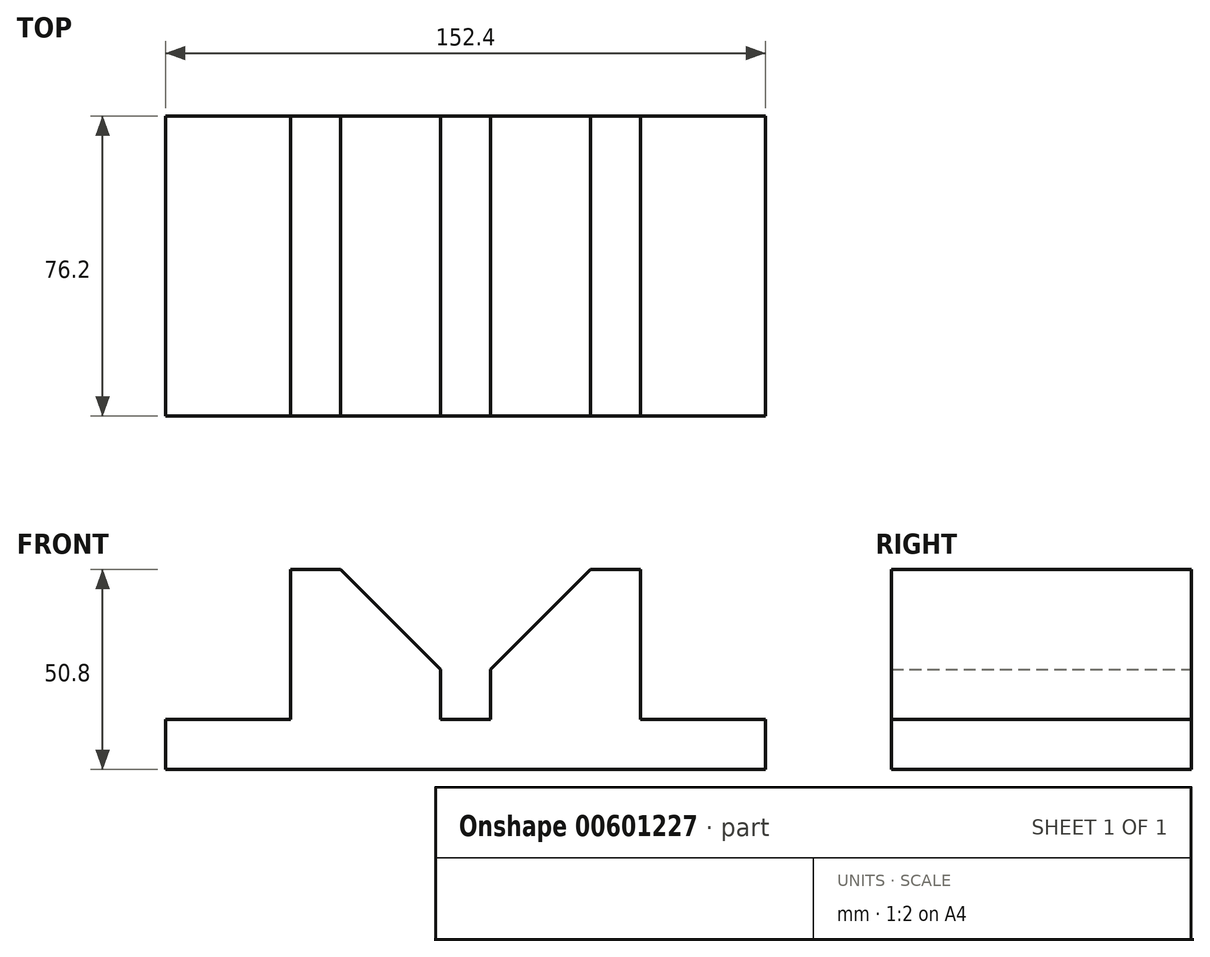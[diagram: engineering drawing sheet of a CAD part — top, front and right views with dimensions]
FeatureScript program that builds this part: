
annotation { "Feature Type Name" : "Feature", "Feature Type Description" : "" }
export const myFeature = defineFeature(function(context is Context, id is Id, definition is map)
    precondition{}
    {
        {
            var Q0;
            Q0=qCreatedBy(makeId("Front.planeOp"),FACE);
            var sketch = newSketch(context, id + "F0", { "sketchPlane" : qUnion([Q0])});
            skLineSegment(sketch, "E0", {"start": v(0, 0) * mm, "end": v(152.4, 0) * mm});
            skLineSegment(sketch, "E1", {"start": v(152.4, 0) * mm, "end": v(152.4, 12.7) * mm});
            skLineSegment(sketch, "E2", {"start": v(0, 0) * mm, "end": v(0, 12.7) * mm});
            skLineSegment(sketch, "E3", {"start": v(0, 12.7) * mm, "end": v(31.75, 12.7) * mm});
            skLineSegment(sketch, "E4", {"start": v(152.4, 12.7) * mm, "end": v(120.65, 12.7) * mm});
            skLineSegment(sketch, "E5", {"start": v(31.75, 12.7) * mm, "end": v(31.75, 50.8) * mm});
            skLineSegment(sketch, "E6", {"start": v(120.65, 12.7) * mm, "end": v(120.65, 50.8) * mm});
            skLineSegment(sketch, "E7", {"start": v(31.75, 50.8) * mm, "end": v(44.45, 50.8) * mm});
            skLineSegment(sketch, "E8", {"start": v(120.65, 50.8) * mm, "end": v(107.95, 50.8) * mm});
            skLineSegment(sketch, "E9", {"start": v(44.45, 50.8) * mm, "end": v(69.85, 25.4) * mm});
            skLineSegment(sketch, "E10", {"start": v(82.55, 25.4) * mm, "end": v(107.95, 50.8) * mm});
            skLineSegment(sketch, "E11", {"start": v(69.85, 25.4) * mm, "end": v(69.85, 12.7) * mm});
            skLineSegment(sketch, "E12", {"start": v(82.55, 25.4) * mm, "end": v(82.55, 12.7) * mm});
            skLineSegment(sketch, "E13", {"start": v(82.55, 12.7) * mm, "end": v(69.85, 12.7) * mm});
            skSolve(sketch);
        }
        {
            var Q0;
            Q0=makeQuery(id+"F0.imprint","IMPRINT",FACE,{"disambiguationData":[TD([[makeQuery(id+"F0.imprint","IMPRINT",EDGE,{"derivedFrom":sQuery(id+"F0.wireOp",EDGE,"E0")}),1.0]])]});
            extrude(context, id + "F1", {"entities" : qUnion([Q0]), "depth" : 76.2 * mm, "offsetDistance" : 25.4 * mm});
        }
    });
